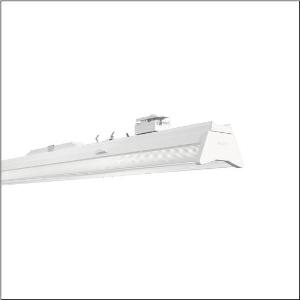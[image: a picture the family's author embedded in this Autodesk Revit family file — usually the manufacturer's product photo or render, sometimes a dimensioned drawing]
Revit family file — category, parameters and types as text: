
# Revit family: licross_r__11_performance_mo_51td16dn4axg_9e80
name_source: partatom
category: Lighting Fixtures
units: mm (PartAtom-declared; Revit-internal decimal feet)

## family parameters
Cut with Voids When Loaded = No
Host = Face
Light Source = No
Part Type = Normal
Room Calculation Point = No
Round Connector Dimension = Use Diameter
Shared = No

## types (1)
- --- (1 x LED, 10110 lm, 57.1 W, 4000K)
    Apparent Load = 57 VA
    CIE Flux Codes = 66 88 96 79 100
    Color Rendering = 80
    Color Temperature = 4000K
    Default Elevation = 1800 mm
    Description = Licross® 11 Performance MO, luminaire insert, of sheet steel, galvanised, coil coated, white, length: 1.500mm, width: 120mm, height: 123mm, LED rated luminous flux: 10.110lm, light colour: 840, control gear: DALI 2, with plug, 5-pole, with phase selection, mains connection: 220..240V, AC, 50/60Hz, rated input power: 57W, halogen-free wiring, primary light control with lens, of plastic, primary optical cover: cover, of PMMA, light emission: direct/indirect distribution, primary light characteristic: symmetric, protection rating (complete): IP54, insulation class (complete): insulation class I (protective earthing), certification: CE, ENEC, VDE, UKCA, protection symbol: D if used in an environment with non-conductive dust loads with corresponding accessories, impact resistance: IK06, permissible ambient temperature for indoor applications: -25..+35°C, corresponds to IFS (International Featured Standards) requirements for safety and quality in the food industry, reducing of maximum allowable ambient temperature of 5°C with ceiling mounting, LABS conformity tested according to VDMA 24364:2018-05, packaging unit: 1 piece
    Height = 114 mm
    Lamp = 1 x LED
    Lamp Light Flux = 10110 lm
    Lamp Power = 57.1 W
    Lamp count = 1
    Length = 1500 mm
    Luminous efficacy = 177 lm/W
    Manufacturer = Siteco
    ModVariant = No
    Model = 51TD16DN4AXG
    Mounting Place = Ceiling
    Mounting Type = Pendant
    Number of Poles = 1
    OnlyDefault = Yes
    Power Factor = 1
    Product Name = Licross® 11 Performance MO
    Product group = luminaire insert
    ProductGroupID = 901
    Protection Class = Protection class I
    Protection Degree = IP 54
    RLX_Detail_Level = 1
    RLX_Emergency_Light_Flux = 0 lm
    RLX_Emergency_Type = 0
    RLX_Emergency_Type_DB = No
    RlxData = <blob elided: 34017 chars, md5=798afb72>
    Socket = socket
    Standby Power = 0 W
    System Light Flux = 10110 lm
    System Power = 57 W
    Type Comments = factory setting: luminous flux: 100 % | dim-lin: 254 | 378 mA
    Type Image = l_1256138.jpg
    URL = http://relux.com
    VarID = @adj_049551
    Voltage = 0 V
    Weight = 0.00 kg
    Width = 120 mm

## geometry (parser evidence)
native form markers: Blend x4, Sweep x11
no freeform markers — native parametric forms only
